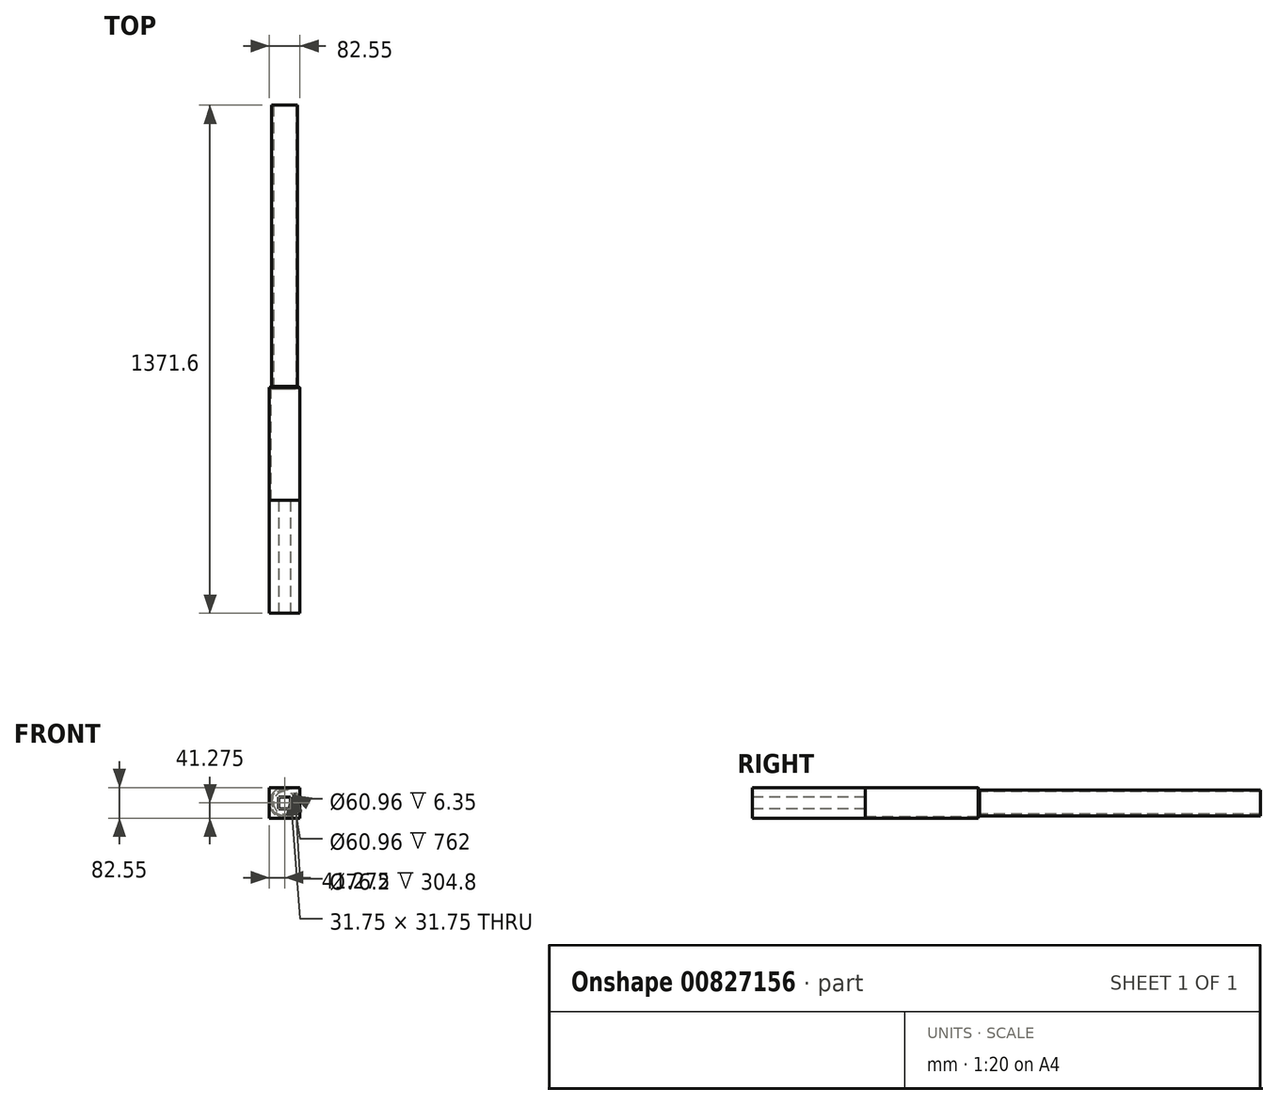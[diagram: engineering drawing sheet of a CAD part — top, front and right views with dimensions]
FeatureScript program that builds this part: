
annotation { "Feature Type Name" : "Feature", "Feature Type Description" : "" }
export const myFeature = defineFeature(function(context is Context, id is Id, definition is map)
    precondition{}
    {
        {
            var Q0;
            Q0=qCreatedBy(makeId("Front.planeOp"),FACE);
            var sketch = newSketch(context, id + "F0", { "sketchPlane" : qUnion([Q0])});
            skLineSegment(sketch, "E0.bottom", {"start": v(0, 0) * mm, "end": v(31.75, 0) * mm});
            skLineSegment(sketch, "E0.top", {"start": v(0, 31.75) * mm, "end": v(31.75, 31.75) * mm});
            skLineSegment(sketch, "E0.left", {"start": v(0, 0) * mm, "end": v(0, 31.75) * mm});
            skLineSegment(sketch, "E0.right", {"start": v(31.75, 0) * mm, "end": v(31.75, 31.75) * mm});
            skPoint(sketch, "E1", {"position": v(57.15, 57.15) * mm});
            skLineSegment(sketch, "E2.bottom", {"start": v(-25.4, -25.4) * mm, "end": v(57.15, -25.4) * mm});
            skLineSegment(sketch, "E2.top", {"start": v(-25.4, 57.15) * mm, "end": v(57.15, 57.15) * mm});
            skLineSegment(sketch, "E2.left", {"start": v(-25.4, -25.4) * mm, "end": v(-25.4, 57.15) * mm});
            skLineSegment(sketch, "E2.right", {"start": v(57.15, -25.4) * mm, "end": v(57.15, 57.15) * mm});
            skSolve(sketch);
        }
        {
            var Q0;
            Q0=makeQuery(id+"F0.imprint","IMPRINT",FACE,{"disambiguationData":[TD([[makeQuery(id+"F0.imprint","IMPRINT",EDGE,{"derivedFrom":sQuery(id+"F0.wireOp",EDGE,"E0.bottom")}),-1.0]])]});
            extrude(context, id + "F1", {"entities" : qUnion([Q0]), "oppositeDirection" : true, "depth" : 304.8 * mm, "offsetDistance" : 25.4 * mm});
        }
        {
            var Q0;
            Q0=makeQuery(id+"F1.opExtrude","CAP_FACE",FACE,{"disambiguationData":[OSD([sQuery(id+"F0.wireOp",EDGE,"E0.bottom"),sQuery(id+"F0.wireOp",EDGE,"E0.top"),sQuery(id+"F0.wireOp",EDGE,"E0.left"),sQuery(id+"F0.wireOp",EDGE,"E0.right"),sQuery(id+"F0.wireOp",EDGE,"E2.bottom"),sQuery(id+"F0.wireOp",EDGE,"E2.top"),sQuery(id+"F0.wireOp",EDGE,"E2.left"),sQuery(id+"F0.wireOp",EDGE,"E2.right")])],"isStart":false});
            var sketch = newSketch(context, id + "F2", { "sketchPlane" : qUnion([Q0])});
            skLineSegment(sketch, "E3", {"start": v(-31.75, 0) * mm, "end": v(0, 31.75) * mm});
            skLineSegment(sketch, "E4", {"start": v(0, 31.75) * mm, "end": v(-31.75, 31.75) * mm});
            skLineSegment(sketch, "E5", {"start": v(-31.75, 31.75) * mm, "end": v(0, 0) * mm});
            skCircle(sketch, "E6", {"center": v(-15.88, 15.88) * mm, "radius": 38.1 * mm});
            skCircle(sketch, "E7", {"center": v(-15.88, 15.88) * mm, "radius": 41.28 * mm});
            skSolve(sketch);
        }
        {
            var Q0;
            Q0=makeQuery(id+"F2.imprint","IMPRINT",FACE,{"disambiguationData":[TD([[makeQuery(id+"F2.imprint","IMPRINT",EDGE,{"derivedFrom":sQuery(id+"F2.wireOp",EDGE,"E6")}),-1.0]])]});
            extrude(context, id + "F3", {"entities" : qUnion([Q0]), "operationType" : NewBodyOperationType.ADD, "depth" : 304.8 * mm, "offsetDistance" : 25.4 * mm});
        }
        {
            var Q0;
            Q0=makeQuery(id+"F3.opExtrude","CAP_FACE",FACE,{"disambiguationData":[OSD([sQuery(id+"F2.wireOp",EDGE,"E6"),sQuery(id+"F2.wireOp",EDGE,"E7")])],"isStart":false});
            var sketch = newSketch(context, id + "F4", { "sketchPlane" : qUnion([Q0])});
            skCircle(sketch, "E8.0.0", {"center": v(-15.88, 15.88) * mm, "radius": 38.1 * mm});
            skLineSegment(sketch, "E9.0", {"start": v(-31.75, 0) * mm, "end": v(-31.75, 31.75) * mm});
            skLineSegment(sketch, "E10.0", {"start": v(0, 31.75) * mm, "end": v(-31.75, 31.75) * mm});
            skCircle(sketch, "E11", {"center": v(-15.88, 15.88) * mm, "radius": 30.48 * mm});
            skCircle(sketch, "E12", {"center": v(-15.88, 15.88) * mm, "radius": 34.93 * mm});
            skSolve(sketch);
        }
        {
            var Q0;
            Q0=makeQuery(id+"F4.imprint","IMPRINT",FACE,{"disambiguationData":[TD([[makeQuery(id+"F4.imprint","IMPRINT",EDGE,{"derivedFrom":sQuery(id+"F4.wireOp",EDGE,"E11")}),-1.0]])]});
            extrude(context, id + "F5", {"entities" : qUnion([Q0]), "depth" : 762 * mm, "offsetDistance" : 25.4 * mm});
        }
        {
            var Q0;
            Q0=makeQuery(id+"F3.opExtrude","CAP_FACE",FACE,{"disambiguationData":[OSD([sQuery(id+"F2.wireOp",EDGE,"E6"),sQuery(id+"F2.wireOp",EDGE,"E7")])],"isStart":false});
            var sketch = newSketch(context, id + "F6", { "sketchPlane" : qUnion([Q0])});
            skCircle(sketch, "E13.0.0", {"center": v(-15.88, 15.88) * mm, "radius": 38.1 * mm});
            skCircle(sketch, "E14", {"center": v(-15.88, 15.88) * mm, "radius": 41.28 * mm});
            skCircle(sketch, "E15", {"center": v(-15.88, 15.88) * mm, "radius": 30.48 * mm});
            skSolve(sketch);
        }
        {
            var Q0;
            Q0=makeQuery(id+"F6.imprint","IMPRINT",FACE,{"disambiguationData":[TD([[makeQuery(id+"F6.imprint","IMPRINT",EDGE,{"derivedFrom":sQuery(id+"F6.wireOp",EDGE,"E13.0.0")}),1.0]])]});
            extrude(context, id + "F7", {"entities" : qUnion([Q0]), "endBound" : BoundingType.SYMMETRIC, "depth" : 6.35 * mm, "offsetDistance" : 25.4 * mm});
        }
    });
